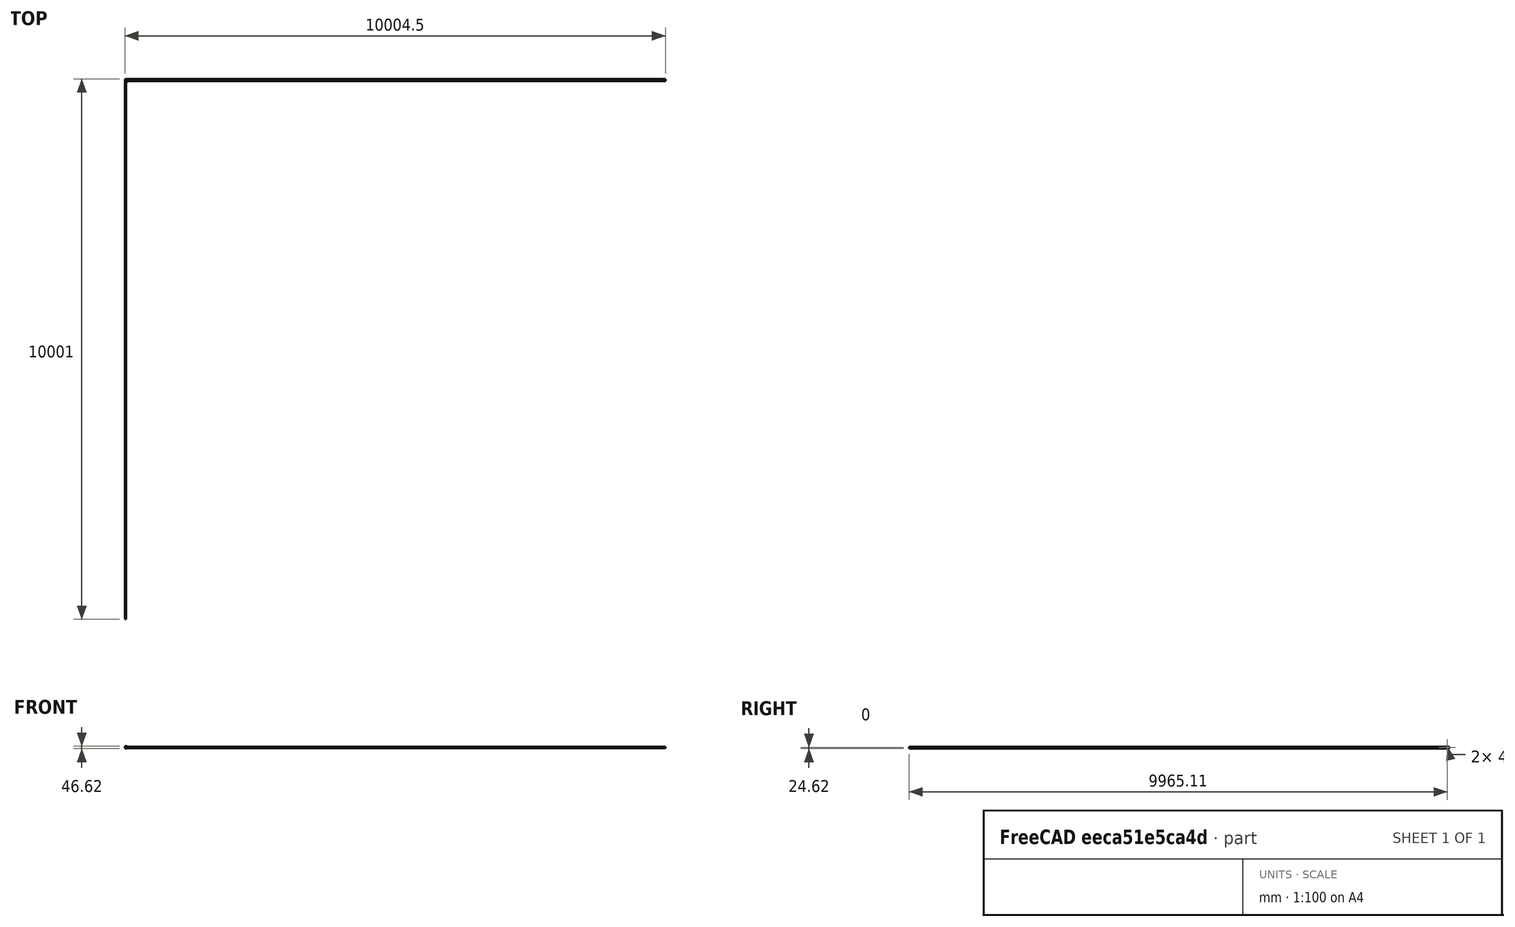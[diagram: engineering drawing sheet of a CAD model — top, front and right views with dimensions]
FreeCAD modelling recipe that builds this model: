
FCSTD DOCUMENT  (FreeCAD 0.15R4671 (Git))
Label: BedLevelBracket
License: All rights reserved
LicenseURL: http://en.wikipedia.org/wiki/All_rights_reserved
objects: Sketcher::SketchObject×8, Part::Feature×5, PartDesign::Pocket×5, Mesh::Feature×3, PartDesign::Pad×3, PartDesign::Fillet×1
note: 30 computed .brp shape members not serialized (recipe doc carries the construction recipe); baked Part::Feature solids carry a one-line shape summary decoded from their .brp

FEATURE [Part::Feature] Part__Feature  label="OB1515_45mm"
  Placement = pos=(-4.5,0,0) rot=(0,0,1;0rad)
  shape: bbox 15 x 15 x 45 mm, 158 faces (baked)
FEATURE [Part::Feature] Part__Feature001  label="BedFoot"
  Placement = pos=(25,12,23) rot=(-1,0,0;1.5708rad)
  shape: bbox 25.43 x 9 x 25.43 mm, 32 faces (baked)
FEATURE [Part::Feature] Part__Feature002  label="BedKnob"
  Placement = pos=(25,2.5,23) rot=(1,0,0;1.5708rad)
  shape: bbox 23.14 x 5 x 23.14 mm, 144 faces (baked)
FEATURE [Mesh::Feature] HexNutStyle1_M
  Placement = pos=(39.2,117,45) rot=(1,0,0;1.5708rad)
FEATURE [Sketcher::SketchObject] Sketch
  Placement = pos=(0,0,0) rot=(0.57735,0.57735,0.57735;2.0944rad)
  sketch-geometry (4):
    g0: LineSegment StartX=-7.5 StartY=40 StartZ=0 EndX=7.46197 EndY=40 EndZ=0
    g1: LineSegment StartX=7.46197 StartY=40 StartZ=0 EndX=7.46197 EndY=6 EndZ=0
    g2: LineSegment StartX=7.46197 StartY=6 StartZ=0 EndX=-7.5 EndY=6 EndZ=0
    g3: LineSegment StartX=-7.5 StartY=6 StartZ=0 EndX=-7.5 EndY=40 EndZ=0
  constraints (8):
    c: Coincident(g0,g1)
    c: Coincident(g1,g2)
    c: Coincident(g2,g3)
    c: Coincident(g3,g0)
    c: Horizontal(g0)
    c: Horizontal(g2)
    c: Vertical(g1)
    c: Vertical(g3)
FEATURE [PartDesign::Pad] Pad
  Length = 32
  Length2 = 100
  Placement = pos=(0,0,0) rot=(0.57735,0.57735,0.57735;2.0944rad)
  Sketch = -> Sketch
  Type = 0
FEATURE [Sketcher::SketchObject] Sketch001
  Placement = pos=(0,0,40) rot=(0,0,-1;1.5708rad)
  Support = -> Pad [Face1]
  sketch-geometry (8):
    g0: LineSegment StartX=-8.5 StartY=7.5 StartZ=0 EndX=11 EndY=7.5 EndZ=0
    g1: LineSegment StartX=11 StartY=7.5 StartZ=0 EndX=11 EndY=-1.61997 EndZ=0
    g2: LineSegment StartX=11 StartY=-1.61997 StartZ=0 EndX=-8.5 EndY=-1.61997 EndZ=0
    g3: LineSegment StartX=-8.5 StartY=-1.61997 StartZ=0 EndX=-8.5 EndY=7.5 EndZ=0
    g4: LineSegment StartX=-2.75 StartY=35.3172 StartZ=0 EndX=2.75 EndY=35.3172 EndZ=0
    g5: LineSegment StartX=2.75 StartY=35.3172 StartZ=0 EndX=2.75 EndY=10.25 EndZ=0
    g6: LineSegment StartX=2.75 StartY=10.25 StartZ=0 EndX=-2.75 EndY=10.25 EndZ=0
    g7: LineSegment StartX=-2.75 StartY=10.25 StartZ=0 EndX=-2.75 EndY=35.3172 EndZ=0
  constraints (16):
    c: Coincident(g0,g1)
    c: Coincident(g1,g2)
    c: Coincident(g2,g3)
    c: Coincident(g3,g0)
    c: Horizontal(g0)
    c: Horizontal(g2)
    c: Vertical(g1)
    c: Vertical(g3)
    c: Coincident(g4,g5)
    c: Coincident(g5,g6)
    c: Coincident(g6,g7)
    c: Coincident(g7,g4)
    c: Horizontal(g4)
    c: Horizontal(g6)
    c: Vertical(g5)
    c: Vertical(g7)
FEATURE [PartDesign::Pocket] Pocket
  Length = 5
  Placement = pos=(0,0,0) rot=(0.57735,0.57735,0.57735;2.0944rad)
  Sketch = -> Sketch001
  Type = 1
FEATURE [Sketcher::SketchObject] Sketch002
  Placement = pos=(0,-7.5,0) rot=(-0.57735,-0.57735,0.57735;4.18879rad)
  Support = -> Pocket [Face9]
  sketch-geometry (10):
    g0: ArcOfCircle CenterX=-23 CenterY=25 CenterZ=0 NormalX=0 NormalY=0 NormalZ=1 Radius=7 StartAngle=0 EndAngle=3.14159
    g1: LineSegment StartX=-16 StartY=25 StartZ=0 EndX=-16 EndY=19 EndZ=0
    g2: LineSegment StartX=-30 StartY=25 StartZ=0 EndX=-30 EndY=19 EndZ=0
    g3: LineSegment StartX=-30 StartY=19 StartZ=0 EndX=-35 EndY=10.25 EndZ=0
    g4: LineSegment StartX=-35 StartY=10.25 StartZ=0 EndX=-41 EndY=10.25 EndZ=0
    g5: LineSegment StartX=-41 StartY=10.25 StartZ=0 EndX=-41 EndY=34 EndZ=0
    g6: LineSegment StartX=-41 StartY=34 StartZ=0 EndX=-5 EndY=34 EndZ=0
    g7: LineSegment StartX=-5 StartY=34 StartZ=0 EndX=-5 EndY=10.25 EndZ=0
    g8: LineSegment StartX=-5 StartY=10.25 StartZ=0 EndX=-11 EndY=10.25 EndZ=0
    g9: LineSegment StartX=-11 StartY=10.25 StartZ=0 EndX=-16 EndY=19 EndZ=0
  constraints (17):
    c: Coincident(g2,g3)
    c: Coincident(g3,g4)
    c: Coincident(g4,g5)
    c: Coincident(g5,g6)
    c: Coincident(g6,g7)
    c: Coincident(g7,g8)
    c: Coincident(g8,g9)
    c: Coincident(g1,g9)
    c: Coincident(g0,g1)
    c: Horizontal(g6)
    c: Horizontal(g8)
    c: Horizontal(g4)
    c: Vertical(g5)
    c: Vertical(g7)
    c: Vertical(g1)
    c: Vertical(g2)
    c: Coincident(g0,g2)
FEATURE [PartDesign::Pocket] Pocket001
  Length = 5
  Placement = pos=(0,0,0) rot=(0.57735,0.57735,0.57735;2.0944rad)
  Sketch = -> Sketch002
  Type = 1
FEATURE [Sketcher::SketchObject] Sketch003
  Placement = pos=(0,-7.5,0) rot=(-0.57735,-0.57735,0.57735;4.18879rad)
  Support = -> Pocket001 [Face3]
  sketch-geometry (1):
    g0: Circle CenterX=-23 CenterY=25 CenterZ=0 NormalX=0 NormalY=0 NormalZ=1 Radius=1.7
  constraints (1):
    c: Radius(g0) = 1.7
FEATURE [PartDesign::Pocket] Pocket002
  Length = 5
  Placement = pos=(0,0,0) rot=(0.57735,0.57735,0.57735;2.0944rad)
  Sketch = -> Sketch003
  Type = 1
FEATURE [Sketcher::SketchObject] Sketch004
  Placement = pos=(7.5,0,0) rot=(0.57735,0.57735,-0.57735;4.18879rad)
  Support = -> Pocket002 [Face5]
  sketch-geometry (4):
    g0: LineSegment StartX=-7.5 StartY=-43 StartZ=0 EndX=7.5 EndY=-43 EndZ=0
    g1: LineSegment StartX=7.5 StartY=-43 StartZ=0 EndX=7.5 EndY=-3 EndZ=0
    g2: LineSegment StartX=7.5 StartY=-3 StartZ=0 EndX=-7.5 EndY=-3 EndZ=0
    g3: LineSegment StartX=-7.5 StartY=-3 StartZ=0 EndX=-7.5 EndY=-43 EndZ=0
  constraints (8):
    c: Coincident(g0,g1)
    c: Coincident(g1,g2)
    c: Coincident(g2,g3)
    c: Coincident(g3,g0)
    c: Horizontal(g0)
    c: Horizontal(g2)
    c: Vertical(g1)
    c: Vertical(g3)
FEATURE [PartDesign::Pad] Pad001
  Length = 5.5
  Length2 = 100
  Midplane = true
  Placement = pos=(0,0,0) rot=(0.57735,0.57735,0.57735;2.0944rad)
  Sketch = -> Sketch004
  Type = 0
FEATURE [Part::Feature] Pad002
  shape: bbox 27.25 x 15 x 40 mm, 21 faces (baked)
FEATURE [Sketcher::SketchObject] Sketch005
  Placement = pos=(10.25,0,0) rot=(0.57735,0.57735,0.57735;2.0944rad)
  Support = -> Pad002 [Face8]
  sketch-geometry (2):
    g0: Circle CenterX=0 CenterY=8 CenterZ=0 NormalX=0 NormalY=0 NormalZ=1 Radius=3.5
    g1: Circle CenterX=0 CenterY=38 CenterZ=0 NormalX=0 NormalY=0 NormalZ=1 Radius=3.5
  constraints (2):
    c: Radius(g0) = 3.5
    c: Equal(g0,g1)
FEATURE [PartDesign::Pocket] Pocket003
  Length = 3
  Sketch = -> Sketch005
  Type = 0
FEATURE [Sketcher::SketchObject] Sketch006
  Placement = pos=(0,-7.5,0) rot=(1,0,0;1.5708rad)
  Support = -> Pocket003 [Face2]
  sketch-geometry (4):
    g0: LineSegment StartX=5 StartY=3 StartZ=0 EndX=3.25 EndY=3 EndZ=0
    g1: LineSegment StartX=3.25 StartY=3 StartZ=0 EndX=3.25 EndY=43 EndZ=0
    g2: LineSegment StartX=3.25 StartY=43 StartZ=0 EndX=5 EndY=43 EndZ=0
    g3: LineSegment StartX=5 StartY=43 StartZ=0 EndX=5 EndY=3 EndZ=0
  constraints (8):
    c: Coincident(g0,g1)
    c: Coincident(g1,g2)
    c: Coincident(g2,g3)
    c: Coincident(g3,g0)
    c: Horizontal(g0)
    c: Horizontal(g2)
    c: Vertical(g1)
    c: Vertical(g3)
FEATURE [PartDesign::Pad] Pad003
  Length = 15
  Length2 = 100
  Reversed = true
  Sketch = -> Sketch006
  Type = 0
FEATURE [Sketcher::SketchObject] Sketch007
  Placement = pos=(7.25,0,0) rot=(0.57735,0.57735,0.57735;2.0944rad)
  Support = -> Pad003 [Face15]
  sketch-geometry (2):
    g0: Circle CenterX=0 CenterY=38 CenterZ=0 NormalX=0 NormalY=0 NormalZ=1 Radius=1.8
    g1: Circle CenterX=0 CenterY=8 CenterZ=0 NormalX=0 NormalY=0 NormalZ=1 Radius=1.8
  constraints (2):
    c: Radius(g1) = 1.8
    c: Equal(g1,g0)
FEATURE [PartDesign::Pocket] Pocket004
  Length = 5
  Sketch = -> Sketch007
  Type = 1
FEATURE [PartDesign::Fillet] Fillet
  Base = -> Pocket004 [Edge40,Edge7,Edge50,Edge13]
  Radius = 4
FEATURE [Part::Feature] Fillet001  label="BedLevelBracket"
  shape: bbox 28.75 x 15 x 40 mm, 31 faces (baked)
FEATURE [Mesh::Feature] SocketHeadCapScrew_M3x  label="SocketHeadCapScrew_M3x25"
  Placement = pos=(32.9,-116,33) rot=(-1,0,0;1.5708rad)
FEATURE [Mesh::Feature] HexNutStyle1_M001
  Placement = pos=(39.2,128,45) rot=(1,0,0;1.5708rad)
